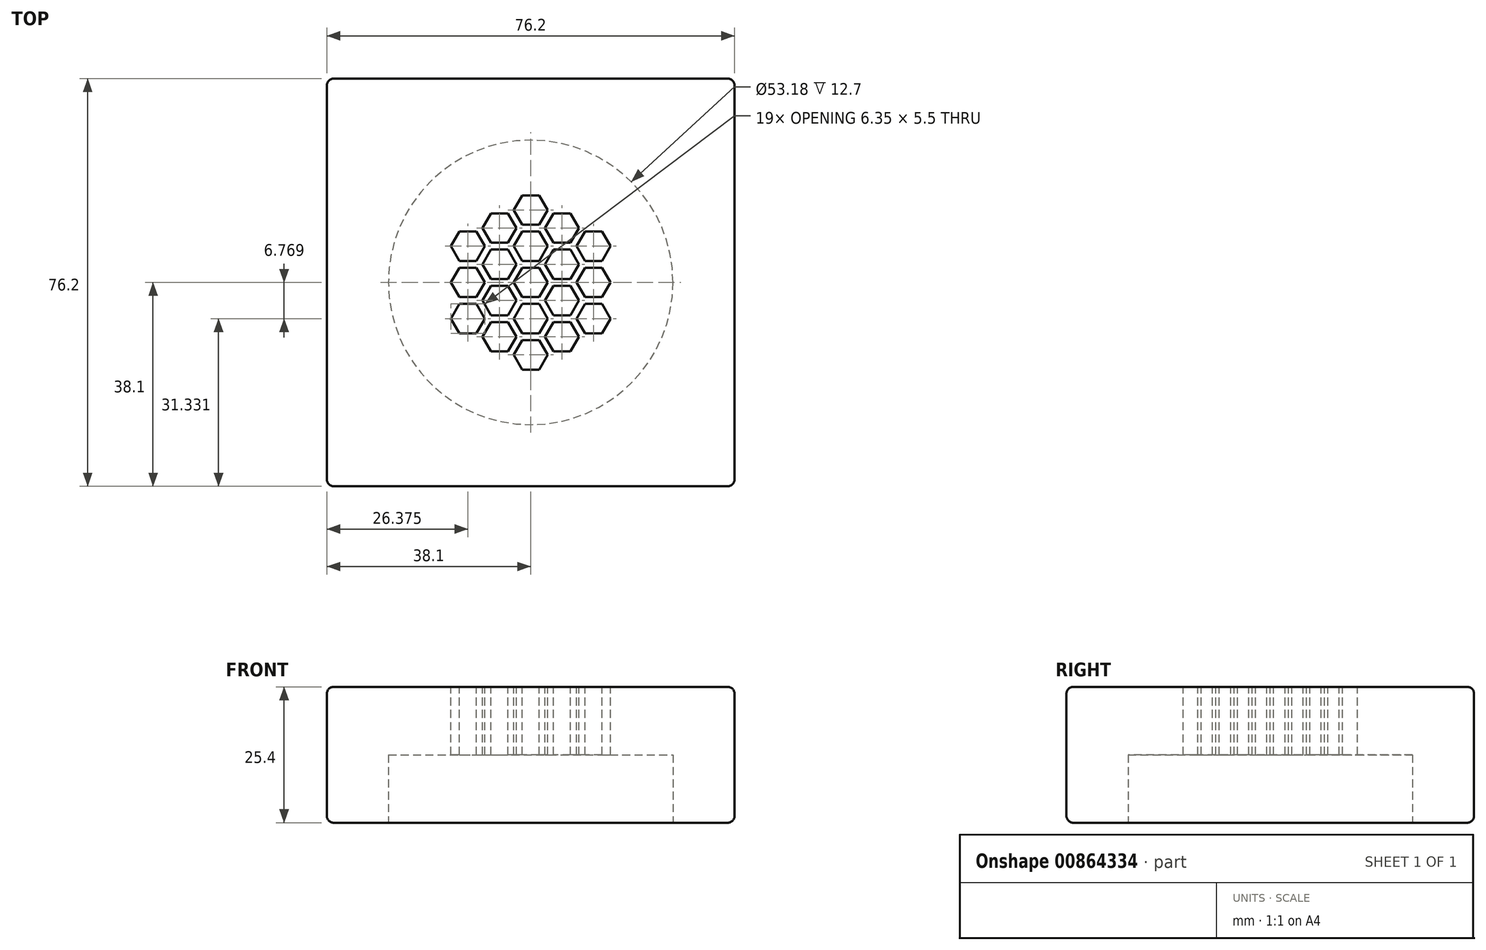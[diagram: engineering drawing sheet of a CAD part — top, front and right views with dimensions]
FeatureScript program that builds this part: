
annotation { "Feature Type Name" : "Feature", "Feature Type Description" : "" }
export const myFeature = defineFeature(function(context is Context, id is Id, definition is map)
    precondition{}
    {
        {
            var Q0;
            Q0=qCreatedBy(makeId("Top.planeOp"),FACE);
            var sketch = newSketch(context, id + "F0", { "sketchPlane" : qUnion([Q0])});
            skLineSegment(sketch, "E0.bottom", {"start": v(38.1, 38.1) * mm, "end": v(-38.1, 38.1) * mm});
            skLineSegment(sketch, "E0.top", {"start": v(38.1, -38.1) * mm, "end": v(-38.1, -38.1) * mm});
            skLineSegment(sketch, "E0.left", {"start": v(38.1, 38.1) * mm, "end": v(38.1, -38.1) * mm});
            skLineSegment(sketch, "E0.right", {"start": v(-38.1, 38.1) * mm, "end": v(-38.1, -38.1) * mm});
            skPoint(sketch, "E0.middle", {"position": v(0, 0) * mm});
            skSolve(sketch);
        }
        {
            var Q0;
            Q0=makeQuery(id+"F0.imprint","IMPRINT",FACE,{"disambiguationData":[TD([[makeQuery(id+"F0.imprint","IMPRINT",EDGE,{"derivedFrom":sQuery(id+"F0.wireOp",EDGE,"E0.bottom")}),1.0]])]});
            extrude(context, id + "F1", {"entities" : qUnion([Q0]), "depth" : 25.4 * mm, "offsetDistance" : 25.4 * mm});
        }
        {
            var Q0;
            Q0=makeQuery(id+"F1.opExtrude","CAP_FACE",FACE,{"disambiguationData":[OSD([sQuery(id+"F0.wireOp",EDGE,"E0.bottom"),sQuery(id+"F0.wireOp",EDGE,"E0.top"),sQuery(id+"F0.wireOp",EDGE,"E0.left"),sQuery(id+"F0.wireOp",EDGE,"E0.right")])],"isStart":true});
            var sketch = newSketch(context, id + "F2", { "sketchPlane" : qUnion([Q0])});
            skCircle(sketch, "E1", {"center": v(0, 0) * mm, "radius": 26.6 * mm});
            skSolve(sketch);
        }
        {
            var Q0;
            Q0=makeQuery(id+"F2.imprint","IMPRINT",FACE,{"disambiguationData":[TD([[makeQuery(id+"F2.imprint","IMPRINT",EDGE,{"derivedFrom":sQuery(id+"F2.wireOp",EDGE,"E1")}),1.0]])]});
            extrude(context, id + "F3", {"entities" : qUnion([Q0]), "operationType" : NewBodyOperationType.REMOVE, "oppositeDirection" : true, "depth" : 12.7 * mm, "offsetDistance" : 25.4 * mm});
        }
        {
            var Q0;
            Q0=makeQuery(id+"F1.opExtrude","CAP_EDGE",EDGE,{"disambiguationData":[OSD([sQuery(id+"F0.wireOp",EDGE,"E0.top")])],"isStart":false});
            var Q1;
            Q1=makeQuery(id+"F1.opExtrude","CAP_EDGE",EDGE,{"disambiguationData":[OSD([sQuery(id+"F0.wireOp",EDGE,"E0.bottom")])],"isStart":false});
            var Q2;
            Q2=makeQuery(id+"F1.opExtrude","CAP_EDGE",EDGE,{"disambiguationData":[OSD([sQuery(id+"F0.wireOp",EDGE,"E0.left")])],"isStart":false});
            var Q3;
            Q3=makeQuery(id+"F1.opExtrude","SWEPT_EDGE",EDGE,{"disambiguationData":[OSD([sQuery(id+"F0.wireOp",EDGE,"E0.top"),sQuery(id+"F0.wireOp",EDGE,"E0.left")])]});
            var Q4;
            Q4=makeQuery(id+"F1.opExtrude","SWEPT_EDGE",EDGE,{"disambiguationData":[OSD([sQuery(id+"F0.wireOp",EDGE,"E0.bottom"),sQuery(id+"F0.wireOp",EDGE,"E0.left")])]});
            var Q5;
            Q5=makeQuery(id+"F1.opExtrude","SWEPT_EDGE",EDGE,{"disambiguationData":[OSD([sQuery(id+"F0.wireOp",EDGE,"E0.bottom"),sQuery(id+"F0.wireOp",EDGE,"E0.right")])]});
            var Q6;
            Q6=makeQuery(id+"F1.opExtrude","SWEPT_EDGE",EDGE,{"disambiguationData":[OSD([sQuery(id+"F0.wireOp",EDGE,"E0.top"),sQuery(id+"F0.wireOp",EDGE,"E0.right")])]});
            var Q7;
            Q7=makeQuery(id+"F1.opExtrude","CAP_EDGE",EDGE,{"disambiguationData":[OSD([sQuery(id+"F0.wireOp",EDGE,"E0.right")])],"isStart":false});
            var Q8;
            Q8=makeQuery(id+"F1.opExtrude","CAP_EDGE",EDGE,{"disambiguationData":[OSD([sQuery(id+"F0.wireOp",EDGE,"E0.top")])],"isStart":true});
            var Q9;
            Q9=makeQuery(id+"F1.opExtrude","CAP_EDGE",EDGE,{"disambiguationData":[OSD([sQuery(id+"F0.wireOp",EDGE,"E0.right")])],"isStart":true});
            var Q10;
            Q10=makeQuery(id+"F1.opExtrude","CAP_EDGE",EDGE,{"disambiguationData":[OSD([sQuery(id+"F0.wireOp",EDGE,"E0.bottom")])],"isStart":true});
            var Q11;
            Q11=makeQuery(id+"F1.opExtrude","CAP_EDGE",EDGE,{"disambiguationData":[OSD([sQuery(id+"F0.wireOp",EDGE,"E0.left")])],"isStart":true});
            fillet(context, id + "F4", {"entities" : qUnion([Q0, Q1, Q2, Q3, Q4, Q5, Q6, Q7, Q8, Q9, Q10, Q11]), "radius" : 1.27 * mm, "tangentPropagation" : true, "allowEdgeOverflow" : false});
        }
        {
            var Q0;
            Q0=makeQuery(id+"F1.opExtrude","CAP_FACE",FACE,{"disambiguationData":[OSD([sQuery(id+"F0.wireOp",EDGE,"E0.bottom"),sQuery(id+"F0.wireOp",EDGE,"E0.top"),sQuery(id+"F0.wireOp",EDGE,"E0.left"),sQuery(id+"F0.wireOp",EDGE,"E0.right")])],"isStart":false});
            var sketch = newSketch(context, id + "F5", { "sketchPlane" : qUnion([Q0])});
            skCircle(sketch, "E2.cCircle", {"center": v(0, 0) * mm, "radius": 3.18 * mm, "construction": true});
            skLineSegment(sketch, "E2.0", {"start": v(3.17, 0) * mm, "end": v(1.59, -2.75) * mm});
            skLineSegment(sketch, "E2.1", {"start": v(1.59, -2.75) * mm, "end": v(-1.59, -2.75) * mm});
            skLineSegment(sketch, "E2.2", {"start": v(-1.59, -2.75) * mm, "end": v(-3.18, 0) * mm});
            skLineSegment(sketch, "E2.3", {"start": v(-3.18, 0) * mm, "end": v(-1.59, 2.75) * mm});
            skLineSegment(sketch, "E2.4", {"start": v(-1.59, 2.75) * mm, "end": v(1.59, 2.75) * mm});
            skLineSegment(sketch, "E2.5", {"start": v(1.59, 2.75) * mm, "end": v(3.17, 0) * mm});
            skLineSegment(sketch, "E3.0", {"start": v(-1.59, 3.38) * mm, "end": v(1.59, 3.38) * mm, "construction": true});
            skLineSegment(sketch, "E4.MirrorCS", {"start": v(-1.59, 4.02) * mm, "end": v(1.59, 4.02) * mm});
            skLineSegment(sketch, "E5.MirrorCS", {"start": v(-3.18, 6.77) * mm, "end": v(-1.59, 4.02) * mm});
            skLineSegment(sketch, "E6.MirrorCS", {"start": v(-1.59, 9.52) * mm, "end": v(-3.18, 6.77) * mm});
            skLineSegment(sketch, "E7.MirrorCS", {"start": v(1.59, 9.52) * mm, "end": v(-1.59, 9.52) * mm});
            skLineSegment(sketch, "E8.MirrorCS", {"start": v(3.17, 6.77) * mm, "end": v(1.59, 9.52) * mm});
            skLineSegment(sketch, "E9.MirrorCS", {"start": v(1.59, 4.02) * mm, "end": v(3.17, 6.77) * mm});
            skLineSegment(sketch, "E10.1.0", {"start": v(-7.45, 0.63) * mm, "end": v(-4.27, 0.63) * mm});
            skLineSegment(sketch, "E10.1.1", {"start": v(-7.45, 6.13) * mm, "end": v(-9.04, 3.38) * mm});
            skLineSegment(sketch, "E10.1.2", {"start": v(-2.69, 3.38) * mm, "end": v(-4.27, 6.13) * mm});
            skLineSegment(sketch, "E10.1.3", {"start": v(-9.04, 3.38) * mm, "end": v(-7.45, 0.63) * mm});
            skLineSegment(sketch, "E10.1.4", {"start": v(-4.27, 6.13) * mm, "end": v(-7.45, 6.13) * mm});
            skLineSegment(sketch, "E10.1.5", {"start": v(-4.27, 0.63) * mm, "end": v(-2.69, 3.38) * mm});
            skLineSegment(sketch, "E10.2.0", {"start": v(-4.27, -6.13) * mm, "end": v(-2.69, -3.38) * mm});
            skLineSegment(sketch, "E10.2.1", {"start": v(-9.04, -3.38) * mm, "end": v(-7.45, -6.13) * mm});
            skLineSegment(sketch, "E10.2.2", {"start": v(-4.27, -0.64) * mm, "end": v(-7.45, -0.64) * mm});
            skLineSegment(sketch, "E10.2.3", {"start": v(-7.45, -6.13) * mm, "end": v(-4.27, -6.13) * mm});
            skLineSegment(sketch, "E10.2.4", {"start": v(-7.45, -0.64) * mm, "end": v(-9.04, -3.38) * mm});
            skLineSegment(sketch, "E10.2.5", {"start": v(-2.69, -3.38) * mm, "end": v(-4.27, -0.63) * mm});
            skLineSegment(sketch, "E11.2.3.0", {"start": v(3.18, -6.77) * mm, "end": v(1.59, -4.02) * mm});
            skLineSegment(sketch, "E11.3.3.0", {"start": v(-1.59, -9.52) * mm, "end": v(1.59, -9.52) * mm});
            skLineSegment(sketch, "E11.6.3.0", {"start": v(-1.59, -4.02) * mm, "end": v(-3.17, -6.77) * mm});
            skLineSegment(sketch, "E11.9.3.0", {"start": v(1.59, -9.52) * mm, "end": v(3.18, -6.77) * mm});
            skLineSegment(sketch, "E11.12.3.0", {"start": v(-3.17, -6.77) * mm, "end": v(-1.59, -9.52) * mm});
            skLineSegment(sketch, "E11.15.3.0", {"start": v(1.59, -4.02) * mm, "end": v(-1.59, -4.02) * mm});
            skLineSegment(sketch, "E11.2.4.0", {"start": v(7.45, -0.64) * mm, "end": v(4.27, -0.64) * mm});
            skLineSegment(sketch, "E11.3.4.0", {"start": v(7.45, -6.13) * mm, "end": v(9.04, -3.38) * mm});
            skLineSegment(sketch, "E11.6.4.0", {"start": v(2.69, -3.38) * mm, "end": v(4.27, -6.13) * mm});
            skLineSegment(sketch, "E11.9.4.0", {"start": v(9.04, -3.38) * mm, "end": v(7.45, -0.63) * mm});
            skLineSegment(sketch, "E11.12.4.0", {"start": v(4.27, -6.13) * mm, "end": v(7.45, -6.13) * mm});
            skLineSegment(sketch, "E11.15.4.0", {"start": v(4.27, -0.63) * mm, "end": v(2.69, -3.38) * mm});
            skLineSegment(sketch, "E11.2.5.0", {"start": v(4.27, 6.13) * mm, "end": v(2.69, 3.38) * mm});
            skLineSegment(sketch, "E11.3.5.0", {"start": v(9.04, 3.38) * mm, "end": v(7.45, 6.13) * mm});
            skLineSegment(sketch, "E11.6.5.0", {"start": v(4.27, 0.64) * mm, "end": v(7.45, 0.64) * mm});
            skLineSegment(sketch, "E11.9.5.0", {"start": v(7.45, 6.13) * mm, "end": v(4.27, 6.13) * mm});
            skLineSegment(sketch, "E11.12.5.0", {"start": v(7.45, 0.64) * mm, "end": v(9.04, 3.38) * mm});
            skLineSegment(sketch, "E11.15.5.0", {"start": v(2.69, 3.38) * mm, "end": v(4.27, 0.64) * mm});
            skLineSegment(sketch, "E12.0", {"start": v(7.45, 6.77) * mm, "end": v(4.27, 6.77) * mm, "construction": true});
            skLineSegment(sketch, "E13.MirrorCS", {"start": v(7.45, 7.4) * mm, "end": v(4.27, 7.4) * mm});
            skLineSegment(sketch, "E14.MirrorCS", {"start": v(4.27, 7.4) * mm, "end": v(2.69, 10.15) * mm});
            skLineSegment(sketch, "E15.MirrorCS", {"start": v(2.69, 10.15) * mm, "end": v(4.27, 12.9) * mm});
            skLineSegment(sketch, "E16.MirrorCS", {"start": v(4.27, 12.9) * mm, "end": v(7.45, 12.9) * mm});
            skLineSegment(sketch, "E17.MirrorCS", {"start": v(7.45, 12.9) * mm, "end": v(9.04, 10.15) * mm});
            skLineSegment(sketch, "E18.MirrorCS", {"start": v(9.04, 10.15) * mm, "end": v(7.45, 7.4) * mm});
            skLineSegment(sketch, "E19.1.0", {"start": v(-9.04, 10.15) * mm, "end": v(-7.45, 12.9) * mm});
            skLineSegment(sketch, "E19.1.1", {"start": v(-7.45, 7.4) * mm, "end": v(-9.04, 10.15) * mm});
            skLineSegment(sketch, "E19.1.2", {"start": v(-4.27, 7.4) * mm, "end": v(-7.45, 7.4) * mm});
            skLineSegment(sketch, "E19.1.3", {"start": v(-2.69, 10.15) * mm, "end": v(-4.27, 7.4) * mm});
            skLineSegment(sketch, "E19.1.4", {"start": v(-4.27, 12.9) * mm, "end": v(-2.69, 10.15) * mm});
            skLineSegment(sketch, "E19.1.5", {"start": v(-7.45, 12.9) * mm, "end": v(-4.27, 12.9) * mm});
            skLineSegment(sketch, "E19.2.0", {"start": v(-13.31, -2.75) * mm, "end": v(-14.9, 0) * mm});
            skLineSegment(sketch, "E19.2.1", {"start": v(-10.14, -2.75) * mm, "end": v(-13.31, -2.75) * mm});
            skLineSegment(sketch, "E19.2.2", {"start": v(-8.55, 0) * mm, "end": v(-10.14, -2.75) * mm});
            skLineSegment(sketch, "E19.2.3", {"start": v(-10.14, 2.75) * mm, "end": v(-8.55, 0) * mm});
            skLineSegment(sketch, "E19.2.4", {"start": v(-13.31, 2.75) * mm, "end": v(-10.14, 2.75) * mm});
            skLineSegment(sketch, "E19.2.5", {"start": v(-14.9, 0) * mm, "end": v(-13.31, 2.75) * mm});
            skLineSegment(sketch, "E20.1.3.0", {"start": v(-4.27, -12.9) * mm, "end": v(-7.45, -12.9) * mm});
            skLineSegment(sketch, "E20.3.3.0", {"start": v(-2.69, -10.15) * mm, "end": v(-4.27, -12.9) * mm});
            skLineSegment(sketch, "E20.6.3.0", {"start": v(-4.27, -7.4) * mm, "end": v(-2.69, -10.15) * mm});
            skLineSegment(sketch, "E20.9.3.0", {"start": v(-7.45, -7.4) * mm, "end": v(-4.27, -7.4) * mm});
            skLineSegment(sketch, "E20.12.3.0", {"start": v(-9.04, -10.15) * mm, "end": v(-7.45, -7.4) * mm});
            skLineSegment(sketch, "E20.15.3.0", {"start": v(-7.45, -12.9) * mm, "end": v(-9.04, -10.15) * mm});
            skLineSegment(sketch, "E20.1.4.0", {"start": v(9.04, -10.15) * mm, "end": v(7.45, -12.9) * mm});
            skLineSegment(sketch, "E20.3.4.0", {"start": v(7.45, -7.4) * mm, "end": v(9.04, -10.15) * mm});
            skLineSegment(sketch, "E20.6.4.0", {"start": v(4.27, -7.4) * mm, "end": v(7.45, -7.4) * mm});
            skLineSegment(sketch, "E20.9.4.0", {"start": v(2.69, -10.15) * mm, "end": v(4.27, -7.4) * mm});
            skLineSegment(sketch, "E20.12.4.0", {"start": v(4.27, -12.9) * mm, "end": v(2.69, -10.15) * mm});
            skLineSegment(sketch, "E20.15.4.0", {"start": v(7.45, -12.9) * mm, "end": v(4.27, -12.9) * mm});
            skLineSegment(sketch, "E20.1.5.0", {"start": v(13.31, 2.75) * mm, "end": v(14.9, 0) * mm});
            skLineSegment(sketch, "E20.3.5.0", {"start": v(10.14, 2.75) * mm, "end": v(13.31, 2.75) * mm});
            skLineSegment(sketch, "E20.6.5.0", {"start": v(8.55, 0) * mm, "end": v(10.14, 2.75) * mm});
            skLineSegment(sketch, "E20.9.5.0", {"start": v(10.14, -2.75) * mm, "end": v(8.55, 0) * mm});
            skLineSegment(sketch, "E20.12.5.0", {"start": v(13.31, -2.75) * mm, "end": v(10.14, -2.75) * mm});
            skLineSegment(sketch, "E20.15.5.0", {"start": v(14.9, 0) * mm, "end": v(13.31, -2.75) * mm});
            skLineSegment(sketch, "E21.0", {"start": v(1.59, 10.15) * mm, "end": v(-1.59, 10.15) * mm, "construction": true});
            skLineSegment(sketch, "E22.MirrorCS", {"start": v(1.59, 10.79) * mm, "end": v(-1.59, 10.79) * mm});
            skLineSegment(sketch, "E23.MirrorCS", {"start": v(-1.59, 10.79) * mm, "end": v(-3.18, 13.54) * mm});
            skLineSegment(sketch, "E24.MirrorCS", {"start": v(-3.18, 13.54) * mm, "end": v(-1.59, 16.29) * mm});
            skLineSegment(sketch, "E25.MirrorCS", {"start": v(-1.59, 16.29) * mm, "end": v(1.59, 16.29) * mm});
            skLineSegment(sketch, "E26.MirrorCS", {"start": v(1.59, 16.29) * mm, "end": v(3.17, 13.54) * mm});
            skLineSegment(sketch, "E27.MirrorCS", {"start": v(3.17, 13.54) * mm, "end": v(1.59, 10.79) * mm});
            skLineSegment(sketch, "E28.1.0", {"start": v(-14.9, 6.77) * mm, "end": v(-13.31, 9.52) * mm});
            skLineSegment(sketch, "E28.1.1", {"start": v(-13.31, 4.02) * mm, "end": v(-14.9, 6.77) * mm});
            skLineSegment(sketch, "E28.1.2", {"start": v(-10.14, 4.02) * mm, "end": v(-13.31, 4.02) * mm});
            skLineSegment(sketch, "E28.1.3", {"start": v(-8.55, 6.77) * mm, "end": v(-10.14, 4.02) * mm});
            skLineSegment(sketch, "E28.1.4", {"start": v(-10.14, 9.52) * mm, "end": v(-8.55, 6.77) * mm});
            skLineSegment(sketch, "E28.1.5", {"start": v(-13.31, 9.52) * mm, "end": v(-10.14, 9.52) * mm});
            skLineSegment(sketch, "E28.2.0", {"start": v(-13.31, -9.52) * mm, "end": v(-14.9, -6.77) * mm});
            skLineSegment(sketch, "E28.2.1", {"start": v(-10.14, -9.52) * mm, "end": v(-13.31, -9.52) * mm});
            skLineSegment(sketch, "E28.2.2", {"start": v(-8.55, -6.77) * mm, "end": v(-10.14, -9.52) * mm});
            skLineSegment(sketch, "E28.2.3", {"start": v(-10.14, -4.02) * mm, "end": v(-8.55, -6.77) * mm});
            skLineSegment(sketch, "E28.2.4", {"start": v(-13.31, -4.02) * mm, "end": v(-10.14, -4.02) * mm});
            skLineSegment(sketch, "E28.2.5", {"start": v(-14.9, -6.77) * mm, "end": v(-13.31, -4.02) * mm});
            skLineSegment(sketch, "E29.1.3.0", {"start": v(1.59, -16.29) * mm, "end": v(-1.59, -16.29) * mm});
            skLineSegment(sketch, "E29.3.3.0", {"start": v(3.18, -13.54) * mm, "end": v(1.59, -16.29) * mm});
            skLineSegment(sketch, "E29.6.3.0", {"start": v(1.59, -10.79) * mm, "end": v(3.18, -13.54) * mm});
            skLineSegment(sketch, "E29.9.3.0", {"start": v(-1.59, -10.79) * mm, "end": v(1.59, -10.79) * mm});
            skLineSegment(sketch, "E29.12.3.0", {"start": v(-3.17, -13.54) * mm, "end": v(-1.59, -10.79) * mm});
            skLineSegment(sketch, "E29.15.3.0", {"start": v(-1.59, -16.29) * mm, "end": v(-3.17, -13.54) * mm});
            skLineSegment(sketch, "E29.1.4.0", {"start": v(14.9, -6.77) * mm, "end": v(13.31, -9.52) * mm});
            skLineSegment(sketch, "E29.3.4.0", {"start": v(13.31, -4.02) * mm, "end": v(14.9, -6.77) * mm});
            skLineSegment(sketch, "E29.6.4.0", {"start": v(10.14, -4.02) * mm, "end": v(13.31, -4.02) * mm});
            skLineSegment(sketch, "E29.9.4.0", {"start": v(8.55, -6.77) * mm, "end": v(10.14, -4.02) * mm});
            skLineSegment(sketch, "E29.12.4.0", {"start": v(10.14, -9.52) * mm, "end": v(8.55, -6.77) * mm});
            skLineSegment(sketch, "E29.15.4.0", {"start": v(13.31, -9.52) * mm, "end": v(10.14, -9.52) * mm});
            skLineSegment(sketch, "E29.1.5.0", {"start": v(13.31, 9.52) * mm, "end": v(14.9, 6.77) * mm});
            skLineSegment(sketch, "E29.3.5.0", {"start": v(10.14, 9.52) * mm, "end": v(13.31, 9.52) * mm});
            skLineSegment(sketch, "E29.6.5.0", {"start": v(8.55, 6.77) * mm, "end": v(10.14, 9.52) * mm});
            skLineSegment(sketch, "E29.9.5.0", {"start": v(10.14, 4.02) * mm, "end": v(8.55, 6.77) * mm});
            skLineSegment(sketch, "E29.12.5.0", {"start": v(13.31, 4.02) * mm, "end": v(10.14, 4.02) * mm});
            skLineSegment(sketch, "E29.15.5.0", {"start": v(14.9, 6.77) * mm, "end": v(13.31, 4.02) * mm});
            skSolve(sketch);
        }
        {
            var Q0;
            Q0 = qSketchRegion(id + "F5", true);
            extrude(context, id + "F6", {"entities" : qUnion([Q0]), "operationType" : NewBodyOperationType.REMOVE, "oppositeDirection" : true, "depth" : 25.4 * mm, "offsetDistance" : 25.4 * mm});
        }
    });
